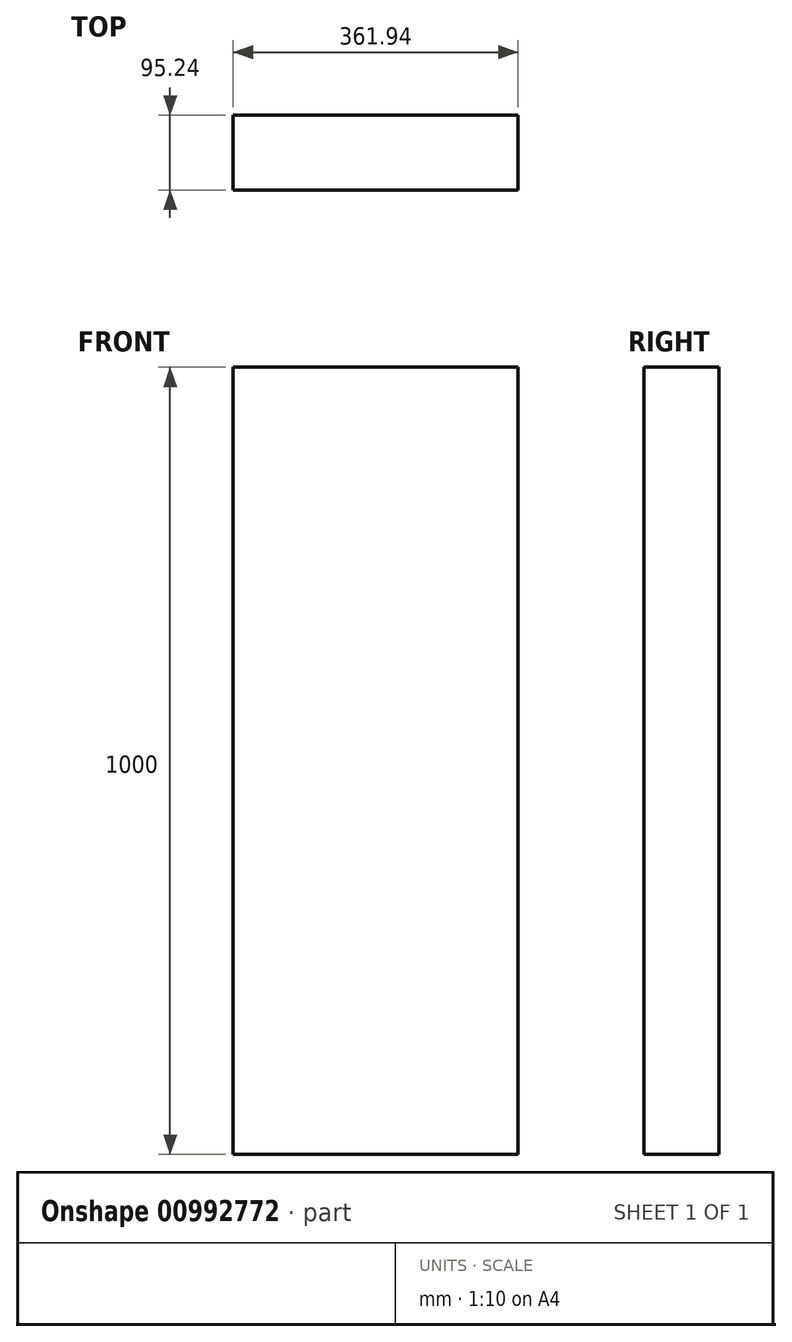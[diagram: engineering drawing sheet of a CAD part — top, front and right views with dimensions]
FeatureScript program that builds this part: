
annotation { "Feature Type Name" : "Feature", "Feature Type Description" : "" }
export const myFeature = defineFeature(function(context is Context, id is Id, definition is map)
    precondition{}
    {
        {
            var Q0;
            Q0=qCreatedBy(makeId("Top.planeOp"),FACE);
            var sketch = newSketch(context, id + "F0", { "sketchPlane" : qUnion([Q0])});
            skLineSegment(sketch, "E0.bottom", {"start": v(180.97, -47.62) * mm, "end": v(-180.98, -47.63) * mm});
            skLineSegment(sketch, "E0.top", {"start": v(180.98, 47.63) * mm, "end": v(-180.98, 47.62) * mm});
            skLineSegment(sketch, "E0.left", {"start": v(180.98, -47.62) * mm, "end": v(180.98, 47.63) * mm});
            skLineSegment(sketch, "E0.right", {"start": v(-180.98, -47.63) * mm, "end": v(-180.98, 47.63) * mm});
            skPoint(sketch, "E0.middle", {"position": v(0, 0) * mm});
            skSolve(sketch);
        }
        {
            var Q0;
            Q0 = qSketchRegion(id + "F0", true);
            extrude(context, id + "F1", {"entities" : qUnion([Q0]), "depth" : 1000 * mm, "offsetDistance" : 25.4 * mm});
        }
    });
